# Revit family: Halter Holorib
name_source: partatom
category: HLS-Bauteile
revit_build: Autodesk Revit 2017 (Build: 20190507_1515(x64)
units: mm (PartAtom-declared; Revit-internal decimal feet)

## family parameters
Basisbauteil = Fläche
Beim Laden mit Abzugskörper schneiden = Nein
Bemaßung runder Anschluss = Durchmesser verwenden
Gemeinsam genutzt = Ja
Raumberechnungspunkt = Nein
Teiletyp = Normal

## types (1)
- Halter Holorib
    Artikelnummer = 08197000
    Ausrichtung Platte = quadratisch
    Befestigung = Verbunddecken
    Breite Platte = 200 mm  [stored 0.656168 ft]
    EAN = 4250928420688
    Fabrikat = MEFA
    Firma = MEFA Befestigungs- und Montagesysteme GmbH
    Gewicht = 3.48 kg
    Gewicht pro Bauteil = 3.48 kg
    Kurztext1 = Halter C-Profil 45 quadratisch
    Kurztext2 = für C-Profil 45/26 - 45/150 fsv
    Langloch = 14x27 mm
    Lochabstand = 150 mm
    Länge = 0 mm  [stored 0 ft]
    Länge Platte = 200 mm  [stored 0.656168 ft]
    Material = Stahl
    Mengeneinheit = St
    Oberflaeche = feuerstückverzinkt
    Profil = C-Profil
    Profilname = 45/26
    Profiltyp = 45/26 - 45/150
    Sicherheitsfaktor = 0
    Stärke Platte = 10 mm  [stored 0.0328084 ft]
    Vorgabe-Ansicht = 1219 mm
    max. Profilhöhe = 150 mm
    max. zul. Last Druck = 0.00 kip
    passend für = Holorib Decke
    vpe = 5 St

note: [stored X ft] marks values corroborated as IEEE doubles in the binary element streams (Revit-internal decimal feet)
